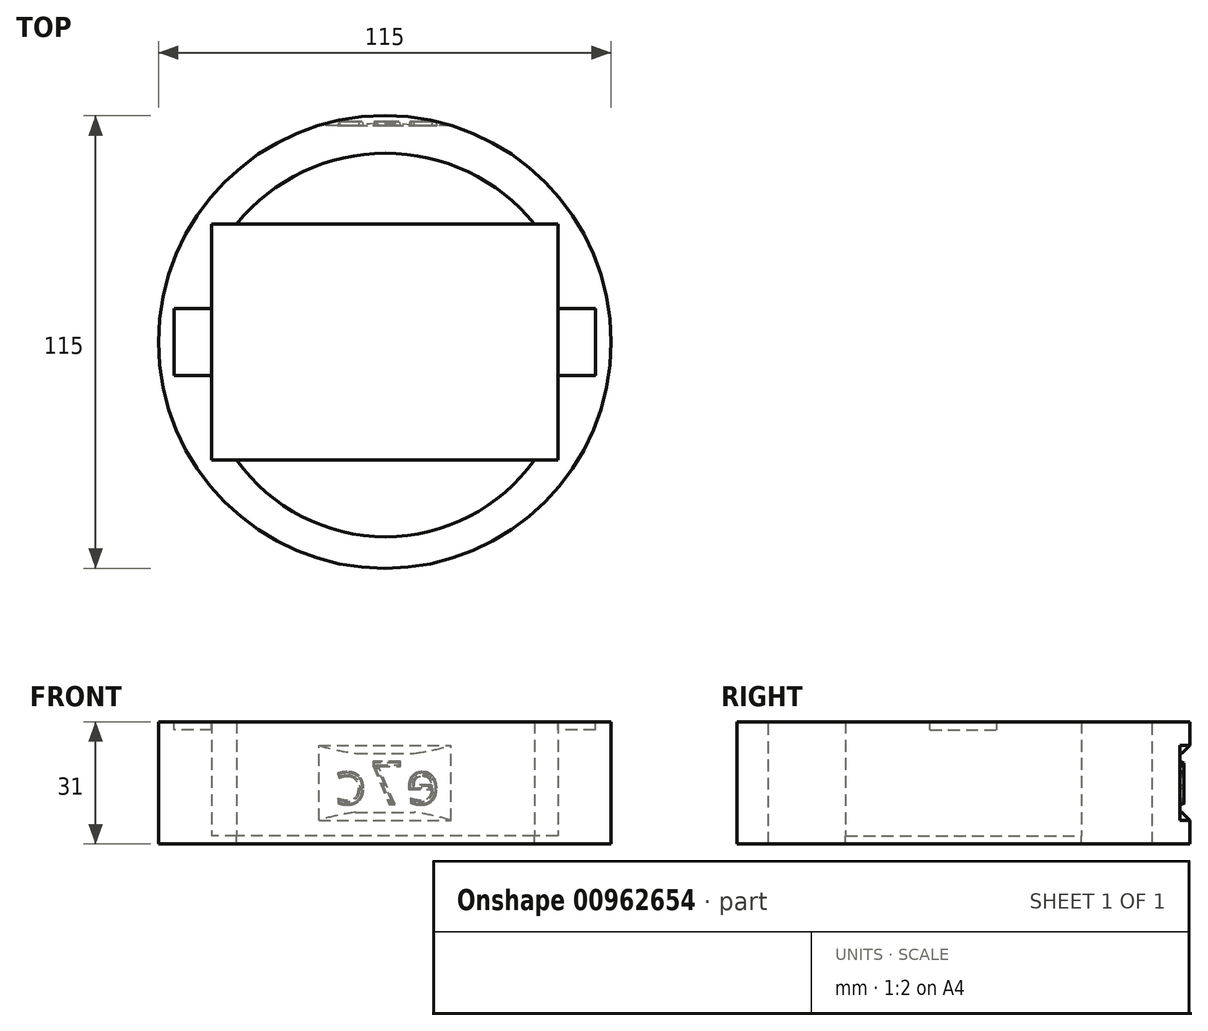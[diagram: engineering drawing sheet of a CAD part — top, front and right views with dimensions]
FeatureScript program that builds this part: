
annotation { "Feature Type Name" : "Feature", "Feature Type Description" : "" }
export const myFeature = defineFeature(function(context is Context, id is Id, definition is map)
    precondition{}
    {
        {
            var Q0;
            Q0=qCreatedBy(makeId("Top.planeOp"),FACE);
            var sketch = newSketch(context, id + "F0", { "sketchPlane" : qUnion([Q0])});
            skLineSegment(sketch, "E0.bottom", {"start": v(44, -30) * mm, "end": v(-44, -30) * mm});
            skLineSegment(sketch, "E0.top", {"start": v(44, 30) * mm, "end": v(-44, 30) * mm});
            skLineSegment(sketch, "E0.left", {"start": v(44, -30) * mm, "end": v(44, 30) * mm});
            skLineSegment(sketch, "E0.right", {"start": v(-44, -30) * mm, "end": v(-44, 30) * mm});
            skPoint(sketch, "E0.middle", {"position": v(0, 0) * mm});
            skCircle(sketch, "E1", {"center": v(0, 0) * mm, "radius": 57.5 * mm});
            skArc(sketch, "E2", {"start": v(37.96, 30) * mm, "mid": v(0.16, 47.98) * mm, "end": v(-37.65, 30) * mm});
            skArc(sketch, "E3", {"start": v(-37.65, -30) * mm, "mid": v(0.16, -49.5) * mm, "end": v(37.96, -30) * mm});
            skSolve(sketch);
        }
        {
            var Q0;
            Q0 = qSketchRegion(id + "F0", true);
            var Q1;
            Q1=makeQuery(id+"F0.imprint","IMPRINT",FACE,{"disambiguationData":[TD([[makeQuery(id+"F0.imprint","IMPRINT",EDGE,{"derivedFrom":sQuery(id+"F0.wireOp",EDGE,"E0.bottom")}),-1.0]])]});
            extrude(context, id + "F1", {"entities" : qUnion([Q0, Q1]), "oppositeDirection" : true, "depth" : 2 * mm, "offsetDistance" : 25 * mm});
        }
        {
            var Q0;
            Q0=makeQuery(id+"F0.imprint","IMPRINT",FACE,{"disambiguationData":[TD([[makeQuery(id+"F0.imprint","IMPRINT",EDGE,{"derivedFrom":sQuery(id+"F0.wireOp",EDGE,"E0.bottom")}),1.0]])]});
            extrude(context, id + "F2", {"entities" : qUnion([Q0]), "operationType" : NewBodyOperationType.ADD, "depth" : 29 * mm, "offsetDistance" : 25 * mm});
        }
        {
            var Q0;
            Q0=makeQuery(id+"F2.opExtrude","CAP_FACE",FACE,{"disambiguationData":[OSD([sQuery(id+"F0.wireOp",EDGE,"E0.bottom"),sQuery(id+"F0.wireOp",EDGE,"E0.top"),sQuery(id+"F0.wireOp",EDGE,"E0.left"),sQuery(id+"F0.wireOp",EDGE,"E0.right"),sQuery(id+"F0.wireOp",EDGE,"E1"),sQuery(id+"F0.wireOp",EDGE,"E2"),sQuery(id+"F0.wireOp",EDGE,"E3")])],"isStart":false});
            var sketch = newSketch(context, id + "F3", { "sketchPlane" : qUnion([Q0])});
            skLineSegment(sketch, "E4.bottom", {"start": v(53.5, -8.5) * mm, "end": v(-53.5, -8.5) * mm});
            skLineSegment(sketch, "E4.top", {"start": v(53.5, 8.5) * mm, "end": v(-53.5, 8.5) * mm});
            skLineSegment(sketch, "E4.left", {"start": v(53.5, -8.5) * mm, "end": v(53.5, 8.5) * mm});
            skLineSegment(sketch, "E4.right", {"start": v(-53.5, -8.5) * mm, "end": v(-53.5, 8.5) * mm});
            skPoint(sketch, "E4.middle", {"position": v(0, 0) * mm});
            skSolve(sketch);
        }
        {
            var Q0;
            {var subQ0=sQuery(id+"F3.wireOp",EDGE,"E4.right");Q0=makeQuery(id+"F3.imprint","IMPRINT",FACE,{"disambiguationData":[TD([[makeQuery(id+"F3.imprint","IMPRINT",EDGE,{"derivedFrom":subQ0}),-1.0]])]});}
            var Q1;
            {var subQ0=sQuery(id+"F3.wireOp",EDGE,"E4.left");Q1=makeQuery(id+"F3.imprint","IMPRINT",FACE,{"disambiguationData":[TD([[makeQuery(id+"F3.imprint","IMPRINT",EDGE,{"derivedFrom":subQ0}),1.0]])]});}
            extrude(context, id + "F4", {"entities" : qUnion([Q0, Q1]), "operationType" : NewBodyOperationType.REMOVE, "oppositeDirection" : true, "depth" : 2 * mm, "offsetDistance" : 25 * mm});
        }
        {
            var Q0;
            Q0=qCreatedBy(makeId("Front.planeOp"),FACE);
            cPlane(context, id + "F5", {"entities" : qUnion([Q0]), "cplaneType" : CPlaneType.OFFSET, "offset" : 55 * mm, "oppositeDirection" : true, "width" : 150 * mm, "height" : 150 * mm});
        }
        {
            var Q0;
            Q0=qCreatedBy(id+"F5.planeOp",FACE);
            var sketch = newSketch(context, id + "F6", { "sketchPlane" : qUnion([Q0])});
            skLineSegment(sketch, "E5.bottom", {"start": v(-23.34, 6) * mm, "end": v(23.34, 6) * mm});
            skLineSegment(sketch, "E5.top", {"start": v(-23.34, 21) * mm, "end": v(23.34, 21) * mm});
            skLineSegment(sketch, "E5.left", {"start": v(-23.34, 6) * mm, "end": v(-23.34, 21) * mm});
            skLineSegment(sketch, "E5.right", {"start": v(23.34, 6) * mm, "end": v(23.34, 21) * mm});
            skPoint(sketch, "E5.middle", {"position": v(0, 13.5) * mm});
            skPoint(sketch, "E6", {"position": v(0, 21) * mm});
            skSolve(sketch);
        }
        {
            var Q0;
            Q0=makeQuery(id+"F6.imprint","IMPRINT",FACE,{"disambiguationData":[TD([[makeQuery(id+"F6.imprint","IMPRINT",EDGE,{"derivedFrom":sQuery(id+"F6.wireOp",EDGE,"E5.bottom")}),1.0]])]});
            extrude(context, id + "F7", {"entities" : qUnion([Q0]), "operationType" : NewBodyOperationType.REMOVE, "oppositeDirection" : true, "depth" : 25 * mm, "offsetDistance" : 25 * mm});
        }
        {
            var Q0;
            Q0=makeQuery(id+"F7.boolean.opBoolean","COPY",FACE,{"derivedFrom":makeQuery(id+"F7.opExtrude","CAP_FACE",FACE,{"disambiguationData":[OSD([sQuery(id+"F6.wireOp",EDGE,"E5.bottom"),sQuery(id+"F6.wireOp",EDGE,"E5.top"),sQuery(id+"F6.wireOp",EDGE,"E5.left"),sQuery(id+"F6.wireOp",EDGE,"E5.right")])],"isStart":true})});
            var sketch = newSketch(context, id + "F8", { "sketchPlane" : qUnion([Q0])});
            skText(sketch, "E7", { "text": "e7c", "fontName": "DroidSansMono.ttf"});
            skPoint(sketch, "E8", {"position": v(-16.78, 13.5) * mm});
            skPoint(sketch, "E9", {"position": v(-14.2, 13.5) * mm});
            skPoint(sketch, "E10", {"position": v(0, 21) * mm});
            const initialGuessF8  = {"E7": [-0.0142, 0.008, 1, 0, 0.011]};
            skSetInitialGuess(sketch, initialGuessF8);
            skSolve(sketch);
        }
        {
            var Q0;
            Q0 = qSketchRegion(id + "F8", true);
            extrude(context, id + "F9", {"entities" : qUnion([Q0]), "operationType" : NewBodyOperationType.ADD, "depth" : 1 * mm, "offsetDistance" : 25 * mm, "hasDraft" : true, "draftAngle" : 20 * degree, "draftPullDirection" : true});
        }
        {
            var Q0;
            {var subQ0=sQuery(id+"F0.wireOp",EDGE,"E1");Q0=makeQuery(id+"F7.boolean.opBoolean","INTERSECT",EDGE,{"derivedFrom":[makeQuery(id+"F2.boolean.opBoolean","MERGE",FACE,{"derivedFrom":[makeQuery(id+"F1.opExtrude","SWEPT_FACE",FACE,{"disambiguationData":[OSD([subQ0])]}),makeQuery(id+"F2.opExtrude","SWEPT_FACE",FACE,{"disambiguationData":[OSD([subQ0])]})]}),makeQuery(id+"F7.opExtrude","SWEPT_FACE",FACE,{"disambiguationData":[OSD([sQuery(id+"F6.wireOp",EDGE,"E5.top")])]})]});}
            var Q1;
            {var subQ0=sQuery(id+"F0.wireOp",EDGE,"E1");Q1=makeQuery(id+"F7.boolean.opBoolean","INTERSECT",EDGE,{"derivedFrom":[makeQuery(id+"F2.boolean.opBoolean","MERGE",FACE,{"derivedFrom":[makeQuery(id+"F1.opExtrude","SWEPT_FACE",FACE,{"disambiguationData":[OSD([subQ0])]}),makeQuery(id+"F2.opExtrude","SWEPT_FACE",FACE,{"disambiguationData":[OSD([subQ0])]})]}),makeQuery(id+"F7.opExtrude","SWEPT_FACE",FACE,{"disambiguationData":[OSD([sQuery(id+"F6.wireOp",EDGE,"E5.bottom")])]})]});}
            chamfer(context, id + "F10", {"entities" : qUnion([Q0, Q1]), "width" : 2 * mm, "tangentPropagation" : true});
        }
    });
